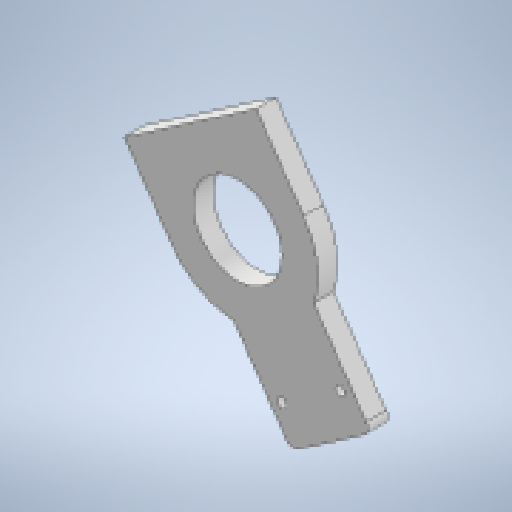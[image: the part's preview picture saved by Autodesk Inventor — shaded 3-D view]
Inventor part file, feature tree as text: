
AUTODESK INVENTOR PART (.ipt)
format: ipt  version: 2024 (Build 280153000, 153)  size: 210,432 bytes
history: native  units: mm
features: other x10, sketch x6, extrude x6, reference x6, fillet x1
ambient origin geometry x8: Origin, YZ Plane, XZ Plane, XY Plane, X Axis, Y Axis, Z Axis, Center Point
bodies: Body1 (feature_tree)
feature tree (29):
  other  "ソリッド1"
  sketch  "スケッチ1"
  other  "作業平面1"
  extrude  "押し出し1"  Depth=10.0mm TaperAngle=0.0deg
  extrude  "押し出し2"  Depth=10.0mm TaperAngle=0.0deg
  extrude  "押し出し3"  Depth=2.2mm
  extrude  "押し出し4"  Depth=2.2mm
  fillet  "フィレット1"  Radius=6.0mm
  extrude  "押し出し5"  Depth=10.0mm TaperAngle=0.0deg
  sketch  "スケッチ6"
  other  "作業平面2"
  extrude  "押し出し6"  Depth=19.0mm
  reference  "参照1"
  reference  "参照2"
  reference  "参照3"
  sketch  "スケッチ2"
  reference  "参照4"
  sketch  "スケッチ3"
  reference  "参照7"
  sketch  "スケッチ4"
  reference  "参照8"
  sketch  "スケッチ5"
  other  "<userpath>\OneDrive\ドキュメント\Inventor\Vixen\leg.iam"
  other  "leg.iam"
  other  "KRS2500_scale:1"
  other  "01029_01042_LowheightServoHorn:1"
  other  "平歯車:1"
  other  "平歯車1:1"
  other  "side_ita:1"
